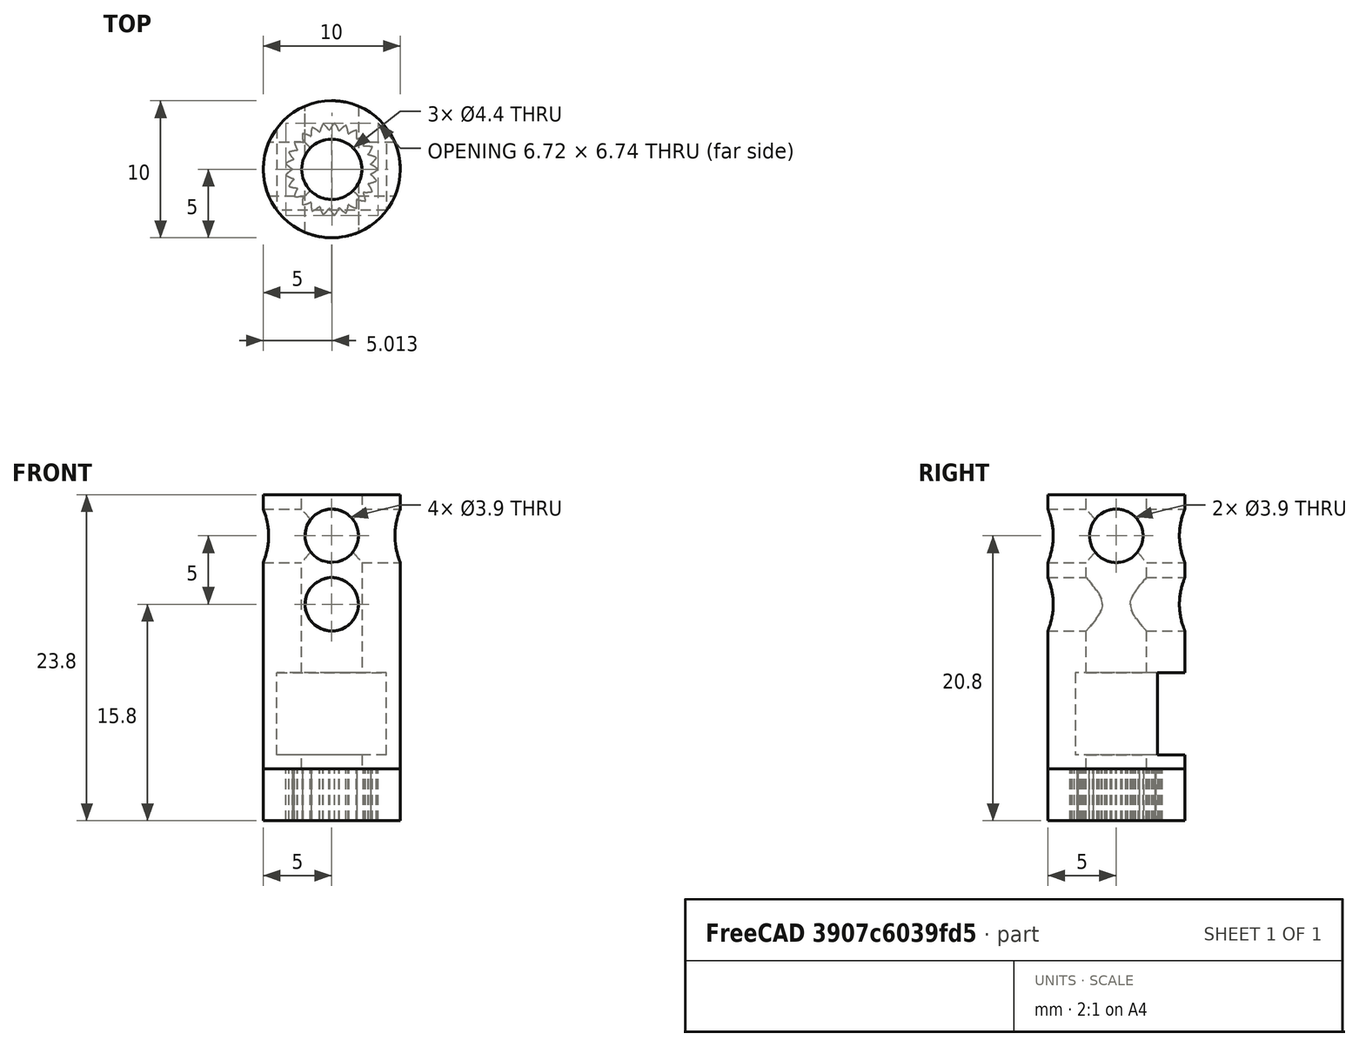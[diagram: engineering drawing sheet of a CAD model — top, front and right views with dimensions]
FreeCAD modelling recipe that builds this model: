
FCSTD DOCUMENT  (FreeCAD 0.18.4R)
Label: servo_cilinder
License: All rights reserved
LicenseURL: http://en.wikipedia.org/wiki/All_rights_reserved
objects: Sketcher::SketchObject×4, PartDesign::Pocket×3, Part::Part2DObjectPython×1, Part::Extrusion×1, Part::Cylinder×1, Part::FeaturePython×1, PartDesign::Pad×1, PartDesign::Body×1
note: 17 computed .brp shape members not serialized (recipe doc carries the construction recipe); baked Part::Feature solids carry a one-line shape summary decoded from their .brp

FEATURE [Part::Part2DObjectPython] InvoluteGear002  # Draft 2D object (typed FeaturePython)
  ExternalGear = true
  HighPrecision = true
  Modules = 0.25
  NumberOfTeeth = 25
  PressureAngle = 36
  expr: Modules = 7 / 28
FEATURE [Part::Extrusion] Extrude002
  Base = -> InvoluteGear002
  Dir = (0,0,1)
  DirMode = 2
  FaceMakerClass = Part::FaceMakerBullseye
  LengthFwd = 3.8
  LengthRev = 0
  Solid = true
  Symmetric = false
FEATURE [Part::Cylinder] Cylinder002
  Angle = 360
  AttacherType = Attacher::AttachEngine3D
  Height = 3.8
  Radius = 5
FEATURE [Part::FeaturePython] Cutout003  # WARN: FeaturePython — macro-defined, semantics opaque (R4)
  Base = -> Cylinder002
  Placement = pos=(-5,-5,-23.8) rot=(0,0,1;0rad)
  Tolerance = 0
  Tool = -> Extrude002
FEATURE [Sketcher::SketchObject] Sketch
  MapMode = 5
  Placement = pos=(0,0,0) rot=(1,0,0;1.5708rad)
  Support = -> [XZ_Plane]
  sketch-geometry (6):
    g0: Circle CenterX=-5 CenterY=-8 CenterZ=0 NormalX=0 NormalY=0 NormalZ=1 AngleXU=0 Radius=1.95
    g1: LineSegment [constr] StartX=-5 StartY=-8 StartZ=0 EndX=-10 EndY=-8 EndZ=0
    g2: LineSegment [constr] StartX=-5 StartY=-8 StartZ=0 EndX=-5 EndY=-20 EndZ=0
    g3: Circle CenterX=-5 CenterY=-3 CenterZ=0 NormalX=0 NormalY=0 NormalZ=1 AngleXU=0 Radius=1.95
    g4: LineSegment [constr] StartX=-5 StartY=-8 StartZ=0 EndX=-5 EndY=-3 EndZ=0
    g5: LineSegment [constr] StartX=-5 StartY=-3 StartZ=0 EndX=-5 EndY=0 EndZ=0
  constraints (17):
    c: Radius(g0) = 1.95
    c: Coincident(g1,g0)
    c: Horizontal(g1)
    c: DistanceX(g1,g1) = 5
    c: Coincident(g2,g0)
    c: Vertical(g2)
    c: DistanceY(g2,g2) = 12
    c: Radius(g3) = 1.95
    c: Coincident(g4,g0)
    c: Coincident(g4,g3)
    c: Vertical(g4)
    c: DistanceY(g4,g4) = 5
    c: Coincident(g5,g3)
    c: PointOnObject(g5,g-1)
    c: Vertical(g5)
    c: DistanceY(g5,g5) = 3
    c: DistanceX(g5,g-1) = 5
FEATURE [Sketcher::SketchObject] Sketch001
  MapMode = 5
  Support = -> [XY_Plane]
  sketch-geometry (3):
    g0: Circle CenterX=-5 CenterY=-5 CenterZ=0 NormalX=0 NormalY=0 NormalZ=1 AngleXU=0 Radius=5
    g1: Circle CenterX=-5 CenterY=-5 CenterZ=0 NormalX=0 NormalY=0 NormalZ=1 AngleXU=0 Radius=2.2
    g2: LineSegment [constr] StartX=-5 StartY=-5 StartZ=0 EndX=0 EndY=-5 EndZ=0
  constraints (8):
    c: Tangent(g0,g-1)
    c: Radius(g0) = 5
    c: Coincident(g1,g0)
    c: Radius(g1) = 2.2
    c: Coincident(g2,g0)
    c: PointOnObject(g2,g-2)
    c: Horizontal(g2)
    c: DistanceX(g2,g2) = 5
FEATURE [PartDesign::Pad] Pad
  Length = 20
  Length2 = 100
  Profile = -> Sketch001
  Reversed = true
  Type = 0
FEATURE [Sketcher::SketchObject] Sketch002
  MapMode = 5
  Placement = pos=(0,0,0) rot=(1,0,0;1.5708rad)
  Support = -> [XZ_Plane]
  sketch-geometry (7):
    g0: LineSegment StartX=-1 StartY=-19 StartZ=0 EndX=-9 EndY=-19 EndZ=0
    g1: LineSegment StartX=-9 StartY=-19 StartZ=0 EndX=-9 EndY=-13 EndZ=0
    g2: LineSegment StartX=-9 StartY=-13 StartZ=0 EndX=-1 EndY=-13 EndZ=0
    g3: LineSegment StartX=-1 StartY=-13 StartZ=0 EndX=-1 EndY=-19 EndZ=0
    g4: LineSegment [constr] StartX=-1 StartY=-13 StartZ=0 EndX=0 EndY=-13 EndZ=0
    g5: LineSegment [constr] StartX=-1 StartY=-19 StartZ=0 EndX=0 EndY=-19 EndZ=0
    g6: LineSegment [constr] StartX=-1 StartY=-13 StartZ=0 EndX=-1 EndY=0 EndZ=0
  constraints (21):
    c: Coincident(g0,g1)
    c: Coincident(g1,g2)
    c: Coincident(g2,g3)
    c: Coincident(g3,g0)
    c: Horizontal(g0)
    c: Vertical(g1)
    c: Vertical(g3)
    c: DistanceY(g3,g3) = 6
    c: DistanceX(g2,g2) = 8
    c: Coincident(g4,g2)
    c: PointOnObject(g4,g-2)
    c: Horizontal(g4)
    c: DistanceX(g4,g4) = 1
    c: Equal(g3,g1)
    c: Coincident(g5,g0)
    c: Horizontal(g5)
    c: Equal(g5,g4)
    c: Coincident(g6,g2)
    c: PointOnObject(g6,g-1)
    c: Vertical(g6)
    c: DistanceY(g6,g6) = 13
FEATURE [PartDesign::Pocket] Pocket
  BaseFeature = -> Pad
  Length = 8
  Length2 = 100
  Profile = -> Sketch002
  Reversed = true
  Type = 0
FEATURE [PartDesign::Pocket] Pocket001
  BaseFeature = -> Pocket
  Length = 5
  Length2 = 100
  Profile = -> Sketch
  Reversed = true
  Type = 1
FEATURE [Sketcher::SketchObject] Sketch003
  MapMode = 5
  Placement = pos=(0,0,0) rot=(0.57735,0.57735,0.57735;2.0944rad)
  Support = -> [YZ_Plane]
  sketch-geometry (2):
    g0: Circle CenterX=-5 CenterY=-3 CenterZ=0 NormalX=0 NormalY=0 NormalZ=1 AngleXU=0 Radius=1.95
    g1: LineSegment [constr] StartX=-5 StartY=-3 StartZ=0 EndX=-5 EndY=0 EndZ=0
  constraints (6):
    c: Radius(g0) = 1.95
    c: Coincident(g1,g0)
    c: PointOnObject(g1,g-1)
    c: Vertical(g1)
    c: DistanceY(g1,g1) = 3
    c: DistanceX(g1,g-1) = 5
FEATURE [PartDesign::Pocket] Pocket002
  BaseFeature = -> Pocket001
  Length = 5
  Length2 = 100
  Profile = -> Sketch003
  Type = 1
FEATURE [PartDesign::Body] Body
  Group = -> [Sketch,Sketch001,Pad,Sketch002,Pocket,Pocket001,Sketch003,Pocket002]
  Origin = -> Origin
  Tip = -> Pocket002
